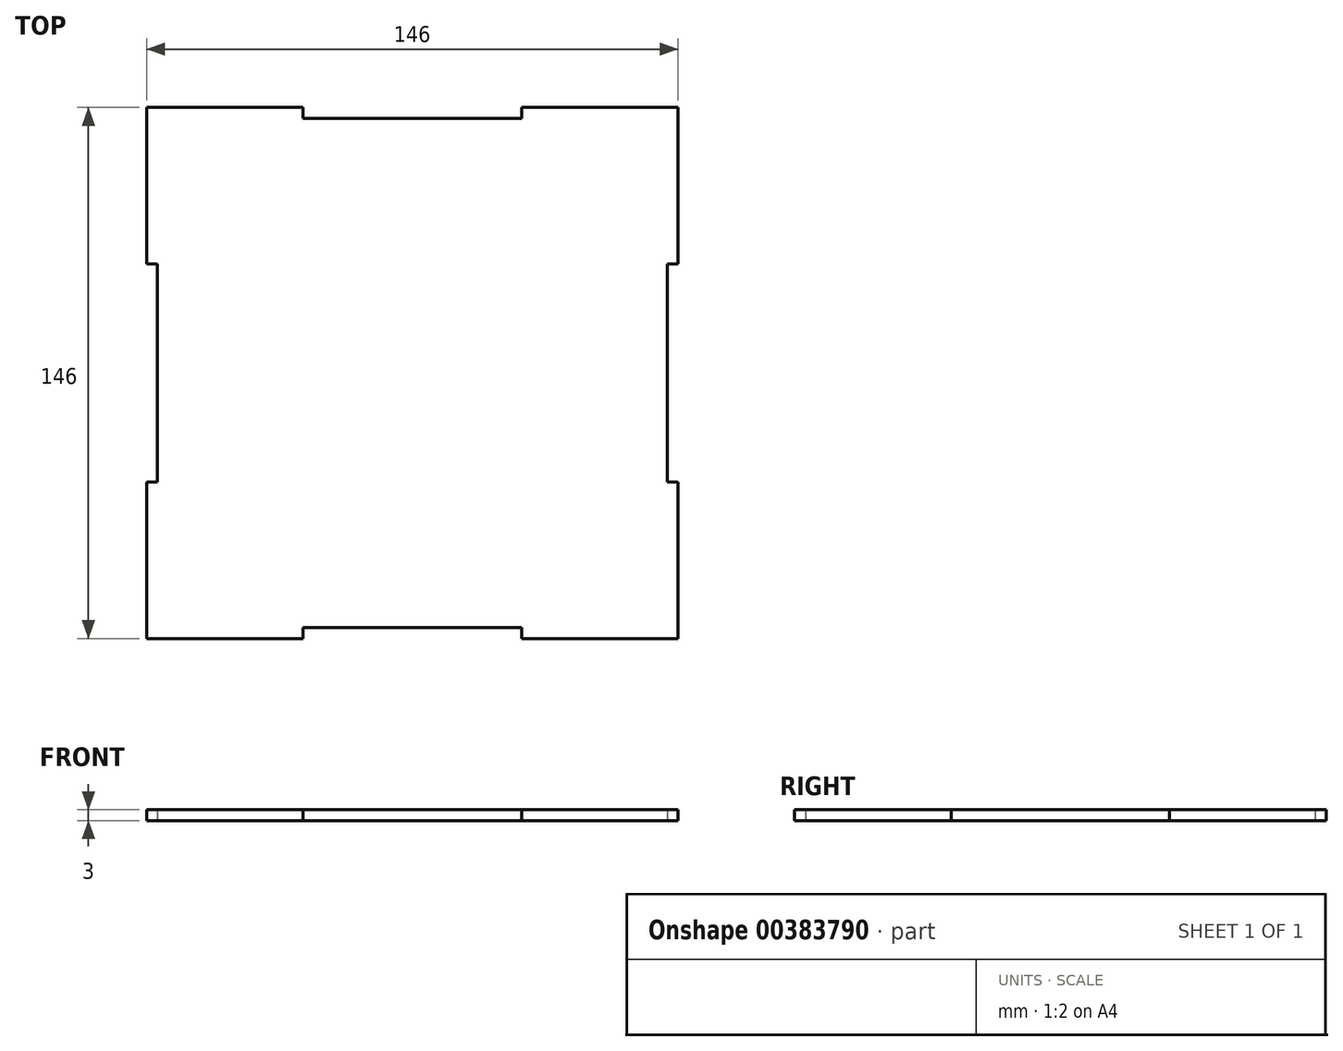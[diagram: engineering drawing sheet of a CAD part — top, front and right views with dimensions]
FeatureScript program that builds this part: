
annotation { "Feature Type Name" : "Feature", "Feature Type Description" : "" }
export const myFeature = defineFeature(function(context is Context, id is Id, definition is map)
    precondition{}
    {
        {
            var Q0;
            Q0=qCreatedBy(makeId("Top.planeOp"),FACE);
            var sketch = newSketch(context, id + "F0", { "sketchPlane" : qUnion([Q0])});
            skLineSegment(sketch, "E0.bottom", {"start": v(73, -73) * mm, "end": v(30, -73) * mm});
            skLineSegment(sketch, "E0.top", {"start": v(73, 73) * mm, "end": v(30, 73) * mm});
            skLineSegment(sketch, "E0.left", {"start": v(73, -73) * mm, "end": v(73, -30) * mm});
            skLineSegment(sketch, "E0.right", {"start": v(-73, -73) * mm, "end": v(-73, -30) * mm});
            skPoint(sketch, "E0.middle", {"position": v(0, 0) * mm});
            skPoint(sketch, "E1.middle", {"position": v(0, 73) * mm});
            skPoint(sketch, "E1.bottom.end.orphan", {"position": v(-30, 70) * mm});
            skPoint(sketch, "E2.orphan", {"position": v(30, 70) * mm});
            skLineSegment(sketch, "E3.trimOffspring", {"start": v(-30, 73) * mm, "end": v(-73, 73) * mm});
            skPoint(sketch, "E4.middle", {"position": v(73, 0) * mm});
            skPoint(sketch, "E5.orphan", {"position": v(70, -30) * mm});
            skPoint(sketch, "E6.orphan", {"position": v(70, 30) * mm});
            skLineSegment(sketch, "E7.trimOffspring", {"start": v(73, 30) * mm, "end": v(73, 73) * mm});
            skPoint(sketch, "E8.middle", {"position": v(0, -73) * mm});
            skPoint(sketch, "E9.orphan", {"position": v(35.3, -67) * mm});
            skPoint(sketch, "E10.orphan", {"position": v(-24.7, -67) * mm});
            skLineSegment(sketch, "E11.trimOffspring", {"start": v(-30, -73) * mm, "end": v(-73, -73) * mm});
            skPoint(sketch, "E12.middle", {"position": v(-73, 0) * mm});
            skPoint(sketch, "E12.right.start.orphan", {"position": v(-70, -30) * mm});
            skPoint(sketch, "E13.orphan", {"position": v(-70, 30) * mm});
            skLineSegment(sketch, "E14.trimOffspring", {"start": v(-73, 30) * mm, "end": v(-73, 73) * mm});
            skLineSegment(sketch, "E15", {"start": v(73, -30) * mm, "end": v(70, -30) * mm});
            skLineSegment(sketch, "E16", {"start": v(70, 30) * mm, "end": v(70, -30) * mm});
            skLineSegment(sketch, "E17", {"start": v(73, 30) * mm, "end": v(70, 30) * mm});
            skPoint(sketch, "E4.top.start.orphan", {"position": v(76, 30) * mm});
            skPoint(sketch, "E4.bottom.start.orphan", {"position": v(76, -30) * mm});
            skLineSegment(sketch, "E18", {"start": v(-30, 73) * mm, "end": v(-30, 70) * mm});
            skLineSegment(sketch, "E19", {"start": v(30, 70) * mm, "end": v(30, 73) * mm});
            skLineSegment(sketch, "E20", {"start": v(30, 70) * mm, "end": v(-30, 70) * mm});
            skPoint(sketch, "E1.right.end.orphan", {"position": v(-30, 76) * mm});
            skPoint(sketch, "E1.left.end.orphan", {"position": v(30, 76) * mm});
            skLineSegment(sketch, "E21", {"start": v(-70, -30) * mm, "end": v(-73, -30) * mm});
            skLineSegment(sketch, "E22", {"start": v(-70, -30) * mm, "end": v(-70, 30) * mm});
            skLineSegment(sketch, "E23", {"start": v(-70, 30) * mm, "end": v(-73, 30) * mm});
            skPoint(sketch, "E12.top.start.orphan", {"position": v(-76, 30) * mm});
            skPoint(sketch, "E12.bottom.start.orphan", {"position": v(-76, -30) * mm});
            skLineSegment(sketch, "E24", {"start": v(-30, -73) * mm, "end": v(-30, -70) * mm});
            skLineSegment(sketch, "E25", {"start": v(-30, -70) * mm, "end": v(30, -70) * mm});
            skLineSegment(sketch, "E26", {"start": v(30, -73) * mm, "end": v(30, -70) * mm});
            skSolve(sketch);
        }
        {
            var Q0;
            Q0=qSketchRegion(id+"F0",true);
            extrude(context, id + "F1", {"entities" : qUnion([Q0]), "depth" : 3 * mm});
        }
    });
